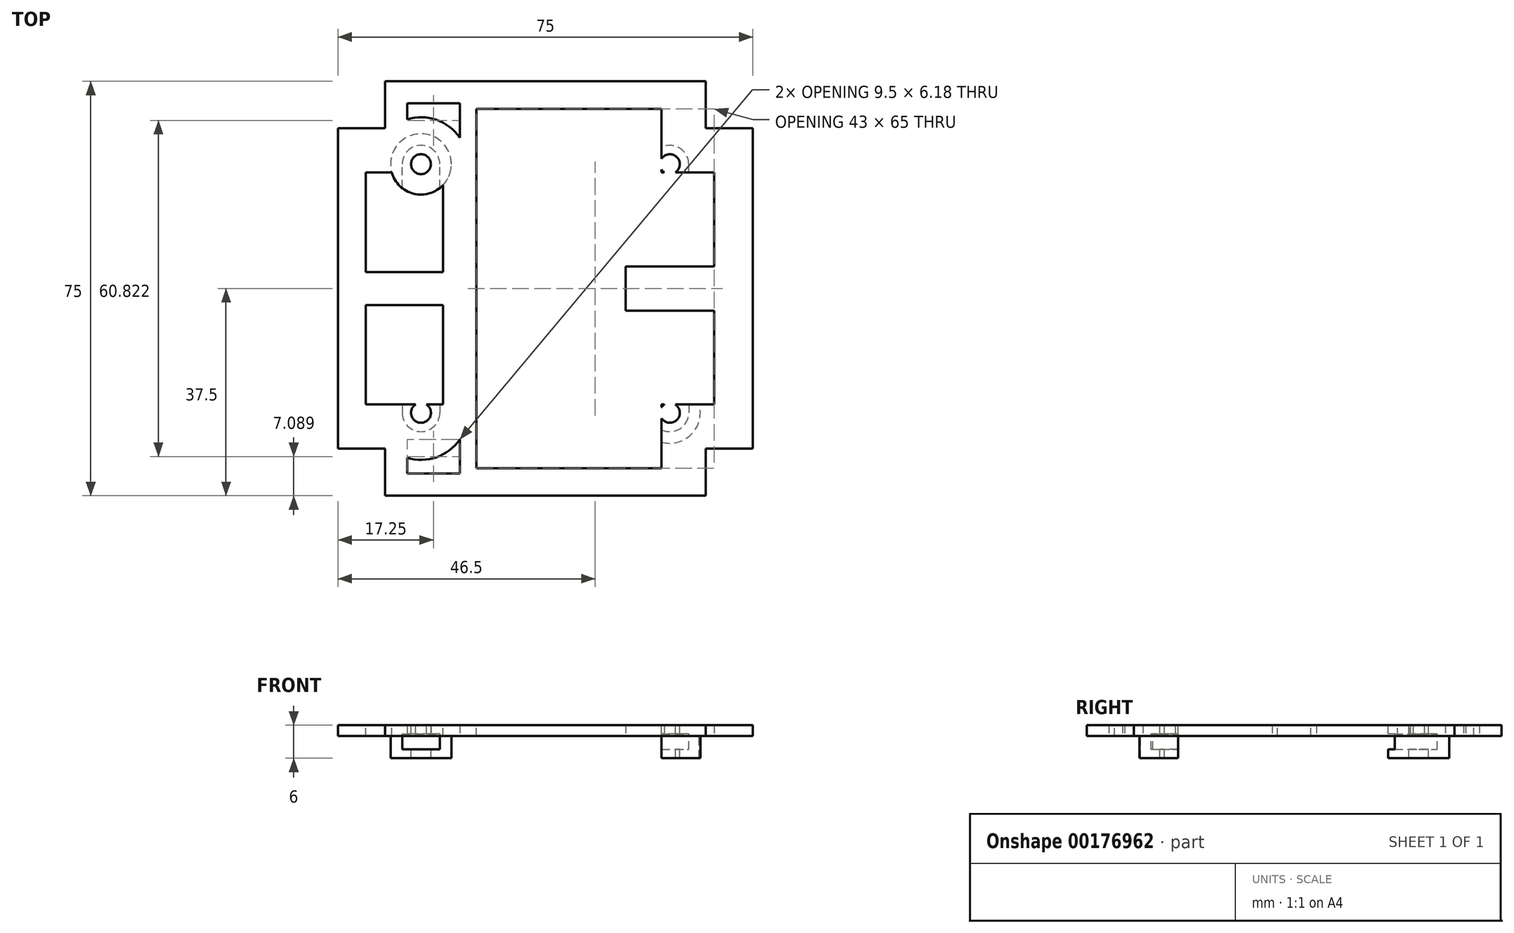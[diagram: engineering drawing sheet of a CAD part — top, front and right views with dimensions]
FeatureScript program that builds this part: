
annotation { "Feature Type Name" : "Feature", "Feature Type Description" : "" }
export const myFeature = defineFeature(function(context is Context, id is Id, definition is map)
    precondition{}
    {
        {
            assignVariable(context, id + "F0", {"name" : "thickness", "anyValue" : 2});
        }
        {
            var Q0;
            Q0=qCreatedBy(makeId("Top.planeOp"),FACE);
            var sketch = newSketch(context, id + "F1", { "sketchPlane" : qUnion([Q0])});
            skLineSegment(sketch, "E0.bottom", {"start": v(29, 37.5) * mm, "end": v(-29, 37.5) * mm});
            skLineSegment(sketch, "E0.top", {"start": v(29, -37.5) * mm, "end": v(-29, -37.5) * mm});
            skLineSegment(sketch, "E0.right", {"start": v(-37.5, 29) * mm, "end": v(-37.5, -29) * mm});
            skPoint(sketch, "E0.middle", {"position": v(0, 0) * mm});
            skLineSegment(sketch, "E1", {"start": v(-37.5, 29) * mm, "end": v(-29, 29) * mm});
            skLineSegment(sketch, "E2", {"start": v(-29, 29) * mm, "end": v(-29, 37.5) * mm});
            skLineSegment(sketch, "E3", {"start": v(0, 0) * mm, "end": v(0, 37.5) * mm, "construction": true});
            skLineSegment(sketch, "E4", {"start": v(0, 0) * mm, "end": v(50, 0) * mm, "construction": true});
            skLineSegment(sketch, "E5.MirrorCS", {"start": v(29, 29) * mm, "end": v(29, 37.5) * mm});
            skLineSegment(sketch, "E6.MirrorCS", {"start": v(37.5, 29) * mm, "end": v(29, 29) * mm});
            skLineSegment(sketch, "E7.MirrorCS", {"start": v(-37.5, -29) * mm, "end": v(-29, -29) * mm});
            skLineSegment(sketch, "E8.MirrorCS", {"start": v(-29, -29) * mm, "end": v(-29, -37.5) * mm});
            skLineSegment(sketch, "E9.MirrorCS", {"start": v(37.5, -29) * mm, "end": v(29, -29) * mm});
            skLineSegment(sketch, "E10.MirrorCS", {"start": v(37.5, -29) * mm, "end": v(37.5, 29) * mm});
            skLineSegment(sketch, "E11.MirrorCS", {"start": v(29, -29) * mm, "end": v(29, -37.5) * mm});
            skSolve(sketch);
        }
        {
            var Q0;
            Q0=makeQuery(id+"F1.imprint","IMPRINT",FACE,{"disambiguationData":[TD([[makeQuery(id+"F1.imprint","IMPRINT",EDGE,{"derivedFrom":sQuery(id+"F1.wireOp",EDGE,"E0.bottom")}),1.0]])]});
            extrude(context, id + "F2", {"entities" : qUnion([Q0]), "depth" : (getVariable(context, 'thickness')) * mm});
        }
        {
            var Q0;
            Q0=makeQuery(id+"F2.opExtrude","CAP_FACE",FACE,{"disambiguationData":[OSD([sQuery(id+"F1.wireOp",EDGE,"E0.bottom"),sQuery(id+"F1.wireOp",EDGE,"E0.right"),sQuery(id+"F1.wireOp",EDGE,"E1"),sQuery(id+"F1.wireOp",EDGE,"E2"),sQuery(id+"F1.wireOp",EDGE,"E5.MirrorCS"),sQuery(id+"F1.wireOp",EDGE,"E6.MirrorCS"),sQuery(id+"F1.wireOp",EDGE,"E7.MirrorCS"),sQuery(id+"F1.wireOp",EDGE,"E8.MirrorCS"),sQuery(id+"F1.wireOp",EDGE,"E9.MirrorCS"),sQuery(id+"F1.wireOp",EDGE,"E10.MirrorCS"),sQuery(id+"F1.wireOp",EDGE,"E11.MirrorCS"),sQuery(id+"F1.wireOp",EDGE,"E0.top"),sQuery(id+"F1.wireOp",EDGE,"QUilWeG3-0awp-yMob-JzGR-0j1FY5nFHNXd")])],"isStart":false});
            var sketch = newSketch(context, id + "F3", { "sketchPlane" : qUnion([Q0])});
            skPoint(sketch, "E12.middle", {"position": v(-6.85, 0) * mm});
            skLineSegment(sketch, "E13.bottom", {"start": v(-12.5, 12) * mm, "end": v(12.5, 12) * mm, "construction": true});
            skLineSegment(sketch, "E13.top", {"start": v(-12.5, -12) * mm, "end": v(12.5, -12) * mm, "construction": true});
            skLineSegment(sketch, "E13.left", {"start": v(-12.5, 12) * mm, "end": v(-12.5, -12) * mm, "construction": true});
            skLineSegment(sketch, "E13.right", {"start": v(12.5, 12) * mm, "end": v(12.5, -12) * mm, "construction": true});
            skPoint(sketch, "E13.middle", {"position": v(0, 0) * mm});
            skLineSegment(sketch, "E14.0", {"start": v(21, -32.5) * mm, "end": v(-12.5, -32.5) * mm});
            skLineSegment(sketch, "E15.0", {"start": v(-32.5, 21) * mm, "end": v(-32.5, 3) * mm});
            skLineSegment(sketch, "E16.0", {"start": v(-32.5, -21) * mm, "end": v(-18.5, -21) * mm});
            skLineSegment(sketch, "E17.MirrorCS", {"start": v(21, 32.5) * mm, "end": v(-12.5, 32.5) * mm});
            skLineSegment(sketch, "E18.MirrorCS", {"start": v(-32.5, 21) * mm, "end": v(-18.5, 21) * mm});
            skLineSegment(sketch, "E19.MirrorCS", {"start": v(30.5, 21) * mm, "end": v(30.5, -21) * mm});
            skLineSegment(sketch, "E20.MirrorCS", {"start": v(30.5, -21) * mm, "end": v(21, -21) * mm});
            skLineSegment(sketch, "E21.MirrorCS", {"start": v(21, -21) * mm, "end": v(21, -32.5) * mm});
            skLineSegment(sketch, "E22", {"start": v(-12.5, -32.5) * mm, "end": v(-12.5, 32.5) * mm});
            skLineSegment(sketch, "E23.0", {"start": v(-18.5, -21) * mm, "end": v(-18.5, -3) * mm});
            skLineSegment(sketch, "E24", {"start": v(-32.5, 3) * mm, "end": v(-18.5, 3) * mm});
            skLineSegment(sketch, "E25.MirrorCS", {"start": v(-32.5, -3) * mm, "end": v(-18.5, -3) * mm});
            skLineSegment(sketch, "E26.trimOffspring", {"start": v(-18.5, 3) * mm, "end": v(-18.5, 21) * mm});
            skLineSegment(sketch, "E27.trimOffspring", {"start": v(-32.5, -3) * mm, "end": v(-32.5, -21) * mm});
            skLineSegment(sketch, "E28.MirrorCS", {"start": v(30.5, 21) * mm, "end": v(21, 21) * mm});
            skLineSegment(sketch, "E29.MirrorCS", {"start": v(21, 21) * mm, "end": v(21, 32.5) * mm});
            skSolve(sketch);
        }
        {
            var Q0;
            Q0=makeQuery(id+"F3.imprint","IMPRINT",FACE,{"disambiguationData":[TD([[makeQuery(id+"F3.imprint","IMPRINT",EDGE,{"derivedFrom":sQuery(id+"F3.wireOp",EDGE,"E15.0")}),1.0]])]});
            var Q1;
            Q1=makeQuery(id+"F3.imprint","IMPRINT",FACE,{"disambiguationData":[TD([[makeQuery(id+"F3.imprint","IMPRINT",EDGE,{"derivedFrom":sQuery(id+"F3.wireOp",EDGE,"E16.0")}),1.0]])]});
            var Q2;
            Q2=makeQuery(id+"F3.imprint","IMPRINT",FACE,{"disambiguationData":[TD([[makeQuery(id+"F3.imprint","IMPRINT",EDGE,{"derivedFrom":sQuery(id+"F3.wireOp",EDGE,"E14.0")}),-1.0]])]});
            extrude(context, id + "F4", {"entities" : qUnion([Q0, Q1, Q2]), "operationType" : NewBodyOperationType.REMOVE, "endBound" : BoundingType.THROUGH_ALL, "oppositeDirection" : true, "depth" : 25 * mm});
        }
        {
            var Q0;
            Q0=makeQuery(id+"F2.opExtrude","CAP_FACE",FACE,{"disambiguationData":[OSD([sQuery(id+"F1.wireOp",EDGE,"E0.bottom"),sQuery(id+"F1.wireOp",EDGE,"E0.right"),sQuery(id+"F1.wireOp",EDGE,"E1"),sQuery(id+"F1.wireOp",EDGE,"E2"),sQuery(id+"F1.wireOp",EDGE,"E5.MirrorCS"),sQuery(id+"F1.wireOp",EDGE,"E6.MirrorCS"),sQuery(id+"F1.wireOp",EDGE,"E7.MirrorCS"),sQuery(id+"F1.wireOp",EDGE,"E8.MirrorCS"),sQuery(id+"F1.wireOp",EDGE,"E9.MirrorCS"),sQuery(id+"F1.wireOp",EDGE,"E10.MirrorCS"),sQuery(id+"F1.wireOp",EDGE,"E11.MirrorCS"),sQuery(id+"F1.wireOp",EDGE,"E0.top"),sQuery(id+"F1.wireOp",EDGE,"QUilWeG3-0awp-yMob-JzGR-0j1FY5nFHNXd")])],"isStart":false});
            var sketch = newSketch(context, id + "F5", { "sketchPlane" : qUnion([Q0])});
            skCircle(sketch, "E30", {"center": v(-22.5, 22.5) * mm, "radius": 1.8 * mm});
            skCircle(sketch, "E31", {"center": v(-22.5, 22.5) * mm, "radius": 5.5 * mm});
            skCircle(sketch, "E32.MirrorC", {"center": v(-22.5, -22.5) * mm, "radius": 1.8 * mm});
            skCircle(sketch, "E33.MirrorC", {"center": v(-22.5, -22.5) * mm, "radius": 5.5 * mm});
            skCircle(sketch, "E34.MirrorC", {"center": v(22.5, 22.5) * mm, "radius": 1.8 * mm});
            skCircle(sketch, "E35.MirrorC", {"center": v(22.5, 22.5) * mm, "radius": 5.5 * mm});
            skCircle(sketch, "E36.MirrorC", {"center": v(22.5, -22.5) * mm, "radius": 5.5 * mm});
            skCircle(sketch, "E37.MirrorC", {"center": v(22.5, -22.5) * mm, "radius": 1.8 * mm});
            skSolve(sketch);
        }
        {
            var Q0;
            {var subQ0=makeQuery(id+"F4.boolean.opBoolean","COPY",EDGE,{"derivedFrom":makeQuery(id+"F4.opExtrude","CAP_EDGE",EDGE,{"disambiguationData":[OSD([sQuery(id+"F3.wireOp",EDGE,"E18.MirrorCS")])],"isStart":true})});var subQ3=sQuery(id+"F5.wireOp",EDGE,"E30");var subQ9=makeQuery(id+"F5.imprint","INTERSECT",VERTEX,{"disambiguationData":[OD(0.0)],"derivedFrom":[subQ0,subQ3]});Q0=makeQuery(id+"F5.imprint","IMPRINT",FACE,{"disambiguationData":[TD([[makeQuery(id+"F5.imprint","IMPRINT",EDGE,{"disambiguationData":[TD([[subQ9,-1.0]])],"derivedFrom":subQ3}),-1.0]])]});}
            var Q1;
            {var subQ0=sQuery(id+"F5.wireOp",EDGE,"E30");var subQ1=makeQuery(id+"F4.boolean.opBoolean","COPY",EDGE,{"derivedFrom":makeQuery(id+"F4.opExtrude","CAP_EDGE",EDGE,{"disambiguationData":[OSD([sQuery(id+"F3.wireOp",EDGE,"E18.MirrorCS")])],"isStart":true})});var subQ2=makeQuery(id+"F5.imprint","INTERSECT",VERTEX,{"disambiguationData":[OD(0.0)],"derivedFrom":[subQ1,subQ0]});Q1=makeQuery(id+"F5.imprint","IMPRINT",FACE,{"disambiguationData":[TD([[makeQuery(id+"F5.imprint","IMPRINT",EDGE,{"disambiguationData":[TD([[subQ2,1.0]])],"derivedFrom":subQ0}),-1.0]])]});}
            var Q2;
            {var subQ0=sQuery(id+"F5.wireOp",EDGE,"E30");var subQ1=makeQuery(id+"F4.boolean.opBoolean","COPY",EDGE,{"derivedFrom":makeQuery(id+"F4.opExtrude","CAP_EDGE",EDGE,{"disambiguationData":[OSD([sQuery(id+"F3.wireOp",EDGE,"E18.MirrorCS")])],"isStart":true})});var subQ2=makeQuery(id+"F5.imprint","INTERSECT",VERTEX,{"disambiguationData":[OD(1.0)],"derivedFrom":[subQ1,subQ0]});Q2=makeQuery(id+"F5.imprint","IMPRINT",FACE,{"disambiguationData":[TD([[makeQuery(id+"F5.imprint","IMPRINT",EDGE,{"disambiguationData":[TD([[subQ2,-1.0]])],"derivedFrom":subQ0}),-1.0]])]});}
            var Q3;
            {var subQ0=sQuery(id+"F5.wireOp",EDGE,"E32.MirrorC");var subQ1=makeQuery(id+"F4.boolean.opBoolean","COPY",EDGE,{"derivedFrom":makeQuery(id+"F4.opExtrude","CAP_EDGE",EDGE,{"disambiguationData":[OSD([sQuery(id+"F3.wireOp",EDGE,"E16.0")])],"isStart":true})});var subQ2=makeQuery(id+"F5.imprint","INTERSECT",VERTEX,{"disambiguationData":[OD(0.0)],"derivedFrom":[subQ1,subQ0]});Q3=makeQuery(id+"F5.imprint","IMPRINT",FACE,{"disambiguationData":[TD([[makeQuery(id+"F5.imprint","IMPRINT",EDGE,{"disambiguationData":[TD([[subQ2,1.0]])],"derivedFrom":subQ0}),1.0]])]});}
            var Q4;
            {var subQ0=sQuery(id+"F5.wireOp",EDGE,"E32.MirrorC");var subQ1=makeQuery(id+"F4.boolean.opBoolean","COPY",EDGE,{"derivedFrom":makeQuery(id+"F4.opExtrude","CAP_EDGE",EDGE,{"disambiguationData":[OSD([sQuery(id+"F3.wireOp",EDGE,"E16.0")])],"isStart":true})});var subQ2=makeQuery(id+"F5.imprint","INTERSECT",VERTEX,{"disambiguationData":[OD(1.0)],"derivedFrom":[subQ1,subQ0]});Q4=makeQuery(id+"F5.imprint","IMPRINT",FACE,{"disambiguationData":[TD([[makeQuery(id+"F5.imprint","IMPRINT",EDGE,{"disambiguationData":[TD([[subQ2,-1.0]])],"derivedFrom":subQ0}),1.0]])]});}
            var Q5;
            {var subQ3=makeQuery(id+"F4.boolean.opBoolean","COPY",EDGE,{"derivedFrom":makeQuery(id+"F4.opExtrude","CAP_EDGE",EDGE,{"disambiguationData":[OSD([sQuery(id+"F3.wireOp",EDGE,"E16.0")])],"isStart":true})});var subQ5=sQuery(id+"F5.wireOp",EDGE,"E32.MirrorC");var subQ9=makeQuery(id+"F5.imprint","INTERSECT",VERTEX,{"disambiguationData":[OD(0.0)],"derivedFrom":[subQ3,subQ5]});Q5=makeQuery(id+"F5.imprint","IMPRINT",FACE,{"disambiguationData":[TD([[makeQuery(id+"F5.imprint","IMPRINT",EDGE,{"disambiguationData":[TD([[subQ9,-1.0]])],"derivedFrom":subQ5}),1.0]])]});}
            var Q6;
            {var subQ0=sQuery(id+"F5.wireOp",EDGE,"E36.MirrorC");var subQ1=makeQuery(id+"F4.boolean.opBoolean","COPY",EDGE,{"derivedFrom":makeQuery(id+"F4.opExtrude","CAP_EDGE",EDGE,{"disambiguationData":[OSD([sQuery(id+"F3.wireOp",EDGE,"E20.MirrorCS")])],"isStart":true})});var subQ2=makeQuery(id+"F5.imprint","INTERSECT",VERTEX,{"derivedFrom":[subQ1,subQ0]});Q6=makeQuery(id+"F5.imprint","IMPRINT",FACE,{"disambiguationData":[TD([[makeQuery(id+"F5.imprint","IMPRINT",EDGE,{"disambiguationData":[TD([[subQ2,1.0]])],"derivedFrom":subQ0}),1.0]])]});}
            var Q7;
            {var subQ0=sQuery(id+"F5.wireOp",EDGE,"E37.MirrorC");var subQ1=makeQuery(id+"F4.boolean.opBoolean","COPY",EDGE,{"derivedFrom":makeQuery(id+"F4.opExtrude","CAP_EDGE",EDGE,{"disambiguationData":[OSD([sQuery(id+"F3.wireOp",EDGE,"E20.MirrorCS")])],"isStart":true})});var subQ2=makeQuery(id+"F5.imprint","INTERSECT",VERTEX,{"disambiguationData":[OD(1.0)],"derivedFrom":[subQ1,subQ0]});Q7=makeQuery(id+"F5.imprint","IMPRINT",FACE,{"disambiguationData":[TD([[makeQuery(id+"F5.imprint","IMPRINT",EDGE,{"disambiguationData":[TD([[subQ2,-1.0]])],"derivedFrom":subQ0}),-1.0]])]});}
            var Q8;
            {var subQ4=makeQuery(id+"F4.boolean.opBoolean","COPY",EDGE,{"derivedFrom":makeQuery(id+"F4.opExtrude","CAP_EDGE",EDGE,{"disambiguationData":[OSD([sQuery(id+"F3.wireOp",EDGE,"E20.MirrorCS")])],"isStart":true})});var subQ8=sQuery(id+"F5.wireOp",EDGE,"E36.MirrorC");var subQ9=makeQuery(id+"F5.imprint","INTERSECT",VERTEX,{"derivedFrom":[subQ4,subQ8]});Q8=makeQuery(id+"F5.imprint","IMPRINT",FACE,{"disambiguationData":[TD([[makeQuery(id+"F5.imprint","IMPRINT",EDGE,{"disambiguationData":[TD([[subQ9,-1.0]])],"derivedFrom":subQ8}),1.0]])]});}
            var Q9;
            {var subQ0=makeQuery(id+"F4.boolean.opBoolean","COPY",EDGE,{"derivedFrom":makeQuery(id+"F4.opExtrude","CAP_EDGE",EDGE,{"disambiguationData":[OSD([sQuery(id+"F3.wireOp",EDGE,"23c06a62-adb4-41f1-888d-e85a26099f890.MirrorCS")])],"isStart":true})});var subQ3=sQuery(id+"F5.wireOp",EDGE,"E34.MirrorC");var subQ9=makeQuery(id+"F5.imprint","INTERSECT",VERTEX,{"disambiguationData":[OD(0.0)],"derivedFrom":[subQ0,subQ3]});Q9=makeQuery(id+"F5.imprint","IMPRINT",FACE,{"disambiguationData":[TD([[makeQuery(id+"F5.imprint","IMPRINT",EDGE,{"disambiguationData":[TD([[subQ9,-1.0]])],"derivedFrom":subQ3}),1.0]])]});}
            var Q10;
            {var subQ0=sQuery(id+"F5.wireOp",EDGE,"E34.MirrorC");var subQ1=makeQuery(id+"F4.boolean.opBoolean","COPY",EDGE,{"derivedFrom":makeQuery(id+"F4.opExtrude","CAP_EDGE",EDGE,{"disambiguationData":[OSD([sQuery(id+"F3.wireOp",EDGE,"23c06a62-adb4-41f1-888d-e85a26099f890.MirrorCS")])],"isStart":true})});var subQ2=makeQuery(id+"F5.imprint","INTERSECT",VERTEX,{"disambiguationData":[OD(0.0)],"derivedFrom":[subQ1,subQ0]});Q10=makeQuery(id+"F5.imprint","IMPRINT",FACE,{"disambiguationData":[TD([[makeQuery(id+"F5.imprint","IMPRINT",EDGE,{"disambiguationData":[TD([[subQ2,1.0]])],"derivedFrom":subQ0}),1.0]])]});}
            var Q11;
            {var subQ0=sQuery(id+"F5.wireOp",EDGE,"E34.MirrorC");var subQ1=makeQuery(id+"F4.boolean.opBoolean","COPY",EDGE,{"derivedFrom":makeQuery(id+"F4.opExtrude","CAP_EDGE",EDGE,{"disambiguationData":[OSD([sQuery(id+"F3.wireOp",EDGE,"23c06a62-adb4-41f1-888d-e85a26099f890.MirrorCS")])],"isStart":true})});var subQ2=makeQuery(id+"F5.imprint","INTERSECT",VERTEX,{"disambiguationData":[OD(1.0)],"derivedFrom":[subQ1,subQ0]});Q11=makeQuery(id+"F5.imprint","IMPRINT",FACE,{"disambiguationData":[TD([[makeQuery(id+"F5.imprint","IMPRINT",EDGE,{"disambiguationData":[TD([[subQ2,-1.0]])],"derivedFrom":subQ0}),1.0]])]});}
            var Q12;
            {var subQ1=makeQuery(id+"F4.boolean.opBoolean","COPY",EDGE,{"derivedFrom":makeQuery(id+"F4.opExtrude","CAP_EDGE",EDGE,{"disambiguationData":[OSD([sQuery(id+"F3.wireOp",EDGE,"E28.MirrorCS")])],"isStart":true})});var subQ3=sQuery(id+"F5.wireOp",EDGE,"E34.MirrorC");var subQ10=makeQuery(id+"F5.imprint","INTERSECT",VERTEX,{"disambiguationData":[OD(0.0)],"derivedFrom":[subQ1,subQ3]});Q12=makeQuery(id+"F5.imprint","IMPRINT",FACE,{"disambiguationData":[TD([[makeQuery(id+"F5.imprint","IMPRINT",EDGE,{"disambiguationData":[TD([[subQ10,-1.0]])],"derivedFrom":subQ3}),1.0]])]});}
            extrude(context, id + "F6", {"entities" : qUnion([Q0, Q1, Q2, Q3, Q4, Q5, Q6, Q7, Q8, Q9, Q10, Q11, Q12]), "operationType" : NewBodyOperationType.ADD, "oppositeDirection" : true, "depth" : 6 * mm});
        }
        {
            var Q0;
            Q0=makeQuery(id+"F6.opExtrude","CAP_FACE",FACE,{"disambiguationData":[OSD([sQuery(id+"F5.wireOp",EDGE,"E30"),sQuery(id+"F5.wireOp",EDGE,"E31")])],"isStart":false});
            var sketch = newSketch(context, id + "F7", { "sketchPlane" : qUnion([Q0])});
            skCircle(sketch, "E38", {"center": v(-22.5, -22.5) * mm, "radius": 1.8 * mm});
            skCircle(sketch, "E39.MirrorC", {"center": v(-22.5, 22.5) * mm, "radius": 1.8 * mm});
            skCircle(sketch, "E40.MirrorC", {"center": v(22.5, -22.5) * mm, "radius": 1.8 * mm});
            skCircle(sketch, "E41.MirrorC", {"center": v(22.5, 22.5) * mm, "radius": 1.8 * mm});
            skSolve(sketch);
        }
        {
            var Q0;
            Q0=qSketchRegion(id+"F7",true);
            extrude(context, id + "F8", {"entities" : qUnion([Q0]), "operationType" : NewBodyOperationType.REMOVE, "endBound" : BoundingType.THROUGH_ALL, "oppositeDirection" : true, "depth" : 25 * mm});
        }
        {
            var Q0;
            {var subQ8=sQuery(id+"F1.wireOp",EDGE,"E1");var subQ9=sQuery(id+"F1.wireOp",EDGE,"E9.MirrorCS");var subQ10=sQuery(id+"F5.wireOp",EDGE,"E31");var subQ11=sQuery(id+"F1.wireOp",EDGE,"E0.top");var subQ12=sQuery(id+"F1.wireOp",EDGE,"E10.MirrorCS");var subQ13=sQuery(id+"F1.wireOp",EDGE,"E11.MirrorCS");var subQ14=sQuery(id+"F1.wireOp",EDGE,"E2");var subQ15=sQuery(id+"F1.wireOp",EDGE,"E0.right");var subQ16=sQuery(id+"F1.wireOp",EDGE,"E0.bottom");var subQ17=sQuery(id+"F1.wireOp",EDGE,"E5.MirrorCS");var subQ18=sQuery(id+"F5.wireOp",EDGE,"E33.MirrorC");var subQ19=sQuery(id+"F1.wireOp",EDGE,"E6.MirrorCS");var subQ20=sQuery(id+"F1.wireOp",EDGE,"E7.MirrorCS");var subQ21=sQuery(id+"F1.wireOp",EDGE,"E8.MirrorCS");var subQ22=sQuery(id+"F5.wireOp",EDGE,"E37.MirrorC");var subQ23=sQuery(id+"F5.wireOp",EDGE,"E30");var subQ24=sQuery(id+"F5.wireOp",EDGE,"E32.MirrorC");var subQ25=sQuery(id+"F5.wireOp",EDGE,"E36.MirrorC");Q0=makeQuery(id+"F8.boolean.opBoolean","SPLIT",FACE,{"disambiguationData":[TD([makeQuery(id+"F2.opExtrude","SWEPT_FACE",FACE,{"disambiguationData":[OSD([subQ16])]})])],"derivedFrom":makeQuery(id+"F6.boolean.opBoolean","MERGE",FACE,{"derivedFrom":[makeQuery(id+"F2.opExtrude","CAP_FACE",FACE,{"disambiguationData":[OSD([subQ16,subQ15,subQ8,subQ14,subQ17,subQ19,subQ20,subQ21,subQ9,subQ12,subQ13,subQ11])],"isStart":false}),makeQuery(id+"F6.opExtrude","CAP_FACE",FACE,{"disambiguationData":[OSD([subQ23,subQ10])],"isStart":true}),makeQuery(id+"F6.opExtrude","CAP_FACE",FACE,{"disambiguationData":[OSD([subQ24,subQ18])],"isStart":true}),makeQuery(id+"F6.opExtrude","CAP_FACE",FACE,{"disambiguationData":[OSD([subQ25,subQ22])],"isStart":true})]})});}
            cPlane(context, id + "F9", {"entities" : qUnion([Q0]), "cplaneType" : CPlaneType.OFFSET, "offset" : 3 * mm, "oppositeDirection" : true, "width" : 150 * mm, "height" : 150 * mm});
        }
        {
            var Q0;
            Q0=qCreatedBy(id+"F9.planeOp",FACE);
            var sketch = newSketch(context, id + "F10", { "sketchPlane" : qUnion([Q0])});
            skCircle(sketch, "E42", {"center": v(22.5, -22.5) * mm, "radius": 3.4 * mm});
            skCircle(sketch, "E43.MirrorC", {"center": v(22.5, 22.5) * mm, "radius": 3.4 * mm});
            skCircle(sketch, "E44.MirrorC", {"center": v(-22.5, -22.5) * mm, "radius": 3.4 * mm});
            skCircle(sketch, "E45.MirrorC", {"center": v(-22.5, 22.5) * mm, "radius": 3.4 * mm});
            skSolve(sketch);
        }
        {
            var Q0;
            Q0 = qSketchRegion(id + "F10", true);
            extrude(context, id + "F11", {"entities" : qUnion([Q0]), "operationType" : NewBodyOperationType.REMOVE, "oppositeDirection" : true, "depth" : 1.4 * mm, "hasSecondDirection" : true, "secondDirectionOppositeDirection" : false, "secondDirectionDepth" : 1.4 * mm});
        }
        {
            var Q0;
            Q0=qCreatedBy(makeId("Front.planeOp"),FACE);
            cPlane(context, id + "F12", {"entities" : qUnion([Q0]), "cplaneType" : CPlaneType.OFFSET, "offset" : 22.5 * mm, "width" : 150 * mm, "height" : 150 * mm});
        }
        {
            var Q0;
            Q0=qCreatedBy(id+"F12.planeOp",FACE);
            var sketch = newSketch(context, id + "F13", { "sketchPlane" : qUnion([Q0])});
            skLineSegment(sketch, "E46.bottom", {"start": v(19.1, 0.4) * mm, "end": v(25.9, 0.4) * mm});
            skLineSegment(sketch, "E46.top", {"start": v(19.1, -2.4) * mm, "end": v(25.9, -2.4) * mm});
            skLineSegment(sketch, "E46.left", {"start": v(19.1, 0.4) * mm, "end": v(19.1, -2.4) * mm});
            skLineSegment(sketch, "E46.right", {"start": v(25.9, 0.4) * mm, "end": v(25.9, -2.4) * mm});
            skPoint(sketch, "E46.middle", {"position": v(22.5, -1) * mm});
            skLineSegment(sketch, "E47", {"start": v(22.5, 2) * mm, "end": v(22.5, -4) * mm, "construction": true});
            skLineSegment(sketch, "E48.MirrorCS", {"start": v(-25.9, 0.4) * mm, "end": v(-25.9, -2.4) * mm});
            skPoint(sketch, "E49.MirrorP", {"position": v(-22.5, -1) * mm});
            skLineSegment(sketch, "E50.MirrorCS", {"start": v(-19.1, 0.4) * mm, "end": v(-25.9, 0.4) * mm});
            skLineSegment(sketch, "E51.MirrorCS", {"start": v(-22.5, 2) * mm, "end": v(-22.5, -4) * mm, "construction": true});
            skLineSegment(sketch, "E52.MirrorCS", {"start": v(-19.1, -2.4) * mm, "end": v(-25.9, -2.4) * mm});
            skLineSegment(sketch, "E53.MirrorCS", {"start": v(-19.1, 0.4) * mm, "end": v(-19.1, -2.4) * mm});
            skSolve(sketch);
        }
        {
            var Q0;
            Q0 = qSketchRegion(id + "F13", true);
            extrude(context, id + "F14", {"entities" : qUnion([Q0]), "operationType" : NewBodyOperationType.REMOVE, "oppositeDirection" : true, "depth" : 8.8 * mm});
        }
        {
            var Q0;
            Q0=qCreatedBy(makeId("Front.planeOp"),FACE);
            cPlane(context, id + "F15", {"entities" : qUnion([Q0]), "cplaneType" : CPlaneType.OFFSET, "offset" : 22.5 * mm, "oppositeDirection" : true, "width" : 150 * mm, "height" : 150 * mm});
        }
        {
            var Q0;
            Q0=qCreatedBy(id+"F15.planeOp",FACE);
            var sketch = newSketch(context, id + "F16", { "sketchPlane" : qUnion([Q0])});
            skLineSegment(sketch, "E54", {"start": v(22.5, 2) * mm, "end": v(22.5, -4) * mm, "construction": true});
            skLineSegment(sketch, "E55.bottom", {"start": v(25.9, 0.4) * mm, "end": v(19.1, 0.4) * mm});
            skLineSegment(sketch, "E55.top", {"start": v(25.9, -2.4) * mm, "end": v(19.1, -2.4) * mm});
            skLineSegment(sketch, "E55.left", {"start": v(25.9, 0.4) * mm, "end": v(25.9, -2.4) * mm});
            skLineSegment(sketch, "E55.right", {"start": v(19.1, 0.4) * mm, "end": v(19.1, -2.4) * mm});
            skPoint(sketch, "E55.middle", {"position": v(22.5, -1) * mm});
            skLineSegment(sketch, "E56.MirrorCS", {"start": v(-25.9, -2.4) * mm, "end": v(-19.1, -2.4) * mm});
            skLineSegment(sketch, "E57.MirrorCS", {"start": v(-19.1, 0.4) * mm, "end": v(-19.1, -2.4) * mm});
            skLineSegment(sketch, "E58.MirrorCS", {"start": v(-22.5, 2) * mm, "end": v(-22.5, -4) * mm, "construction": true});
            skPoint(sketch, "E59.MirrorP", {"position": v(-22.5, -1) * mm});
            skLineSegment(sketch, "E60.MirrorCS", {"start": v(-25.9, 0.4) * mm, "end": v(-19.1, 0.4) * mm});
            skLineSegment(sketch, "E61.MirrorCS", {"start": v(-25.9, 0.4) * mm, "end": v(-25.9, -2.4) * mm});
            skSolve(sketch);
        }
        {
            var Q0;
            Q0 = qSketchRegion(id + "F16", true);
            extrude(context, id + "F17", {"entities" : qUnion([Q0]), "operationType" : NewBodyOperationType.REMOVE, "depth" : 10.3 * mm});
        }
        {
            var Q0;
            Q0=makeQuery(id+"F4.boolean.opBoolean","COPY",FACE,{"derivedFrom":makeQuery(id+"F4.opExtrude","SWEPT_FACE",FACE,{"disambiguationData":[OSD([sQuery(id+"F3.wireOp",EDGE,"E19.MirrorCS")])]})});
            var sketch = newSketch(context, id + "F18", { "sketchPlane" : qUnion([Q0])});
            skLineSegment(sketch, "E62", {"start": v(0, 0) * mm, "end": v(0, 2) * mm, "construction": true});
            skLineSegment(sketch, "E63.bottom", {"start": v(-4, 2) * mm, "end": v(4, 2) * mm});
            skLineSegment(sketch, "E63.top", {"start": v(-4, 0) * mm, "end": v(4, 0) * mm});
            skLineSegment(sketch, "E63.left", {"start": v(-4, 2) * mm, "end": v(-4, 0) * mm});
            skLineSegment(sketch, "E63.right", {"start": v(4, 2) * mm, "end": v(4, 0) * mm});
            skPoint(sketch, "E63.middle", {"position": v(0, 1) * mm});
            skSolve(sketch);
        }
        {
            var Q0;
            Q0 = qSketchRegion(id + "F18", true);
            extrude(context, id + "F19", {"entities" : qUnion([Q0]), "operationType" : NewBodyOperationType.ADD, "depth" : 16 * mm});
        }
        {
            var Q0;
            {var subQ0=sQuery(id+"F1.wireOp",EDGE,"E1");var subQ1=sQuery(id+"F1.wireOp",EDGE,"E9.MirrorCS");var subQ2=sQuery(id+"F1.wireOp",EDGE,"E0.top");var subQ3=sQuery(id+"F1.wireOp",EDGE,"E10.MirrorCS");var subQ4=sQuery(id+"F1.wireOp",EDGE,"E11.MirrorCS");var subQ5=sQuery(id+"F1.wireOp",EDGE,"E2");var subQ6=sQuery(id+"F1.wireOp",EDGE,"E0.right");var subQ7=sQuery(id+"F1.wireOp",EDGE,"E0.bottom");var subQ8=sQuery(id+"F1.wireOp",EDGE,"E5.MirrorCS");var subQ9=sQuery(id+"F1.wireOp",EDGE,"E6.MirrorCS");var subQ10=sQuery(id+"F1.wireOp",EDGE,"E7.MirrorCS");var subQ11=sQuery(id+"F1.wireOp",EDGE,"E8.MirrorCS");Q0=makeQuery(id+"F19.boolean.opBoolean","MERGE",FACE,{"derivedFrom":[makeQuery(id+"F6.boolean.opBoolean","SPLIT",FACE,{"disambiguationData":[TD([makeQuery(id+"F2.opExtrude","SWEPT_FACE",FACE,{"disambiguationData":[OSD([subQ7])]})])],"derivedFrom":makeQuery(id+"F2.opExtrude","CAP_FACE",FACE,{"disambiguationData":[OSD([subQ7,subQ6,subQ0,subQ5,subQ8,subQ9,subQ10,subQ11,subQ1,subQ3,subQ4,subQ2])],"isStart":true})}),makeQuery(id+"F19.opExtrude","SWEPT_FACE",FACE,{"disambiguationData":[OSD([sQuery(id+"F18.wireOp",EDGE,"E63.top")])]})]});}
            var sketch = newSketch(context, id + "F20", { "sketchPlane" : qUnion([Q0])});
            skArc(sketch, "E64.0", {"start": v(-15.5, 27.32) * mm, "mid": v(-19.7, 30.53) * mm, "end": v(-25, 30.62) * mm});
            skLineSegment(sketch, "E65.0", {"start": v(-15.5, 33.5) * mm, "end": v(-15.5, 27.32) * mm});
            skLineSegment(sketch, "E66.0", {"start": v(-15.5, 33.5) * mm, "end": v(-25, 33.5) * mm});
            skLineSegment(sketch, "E67.0", {"start": v(-25, 30.62) * mm, "end": v(-25, 33.5) * mm});
            skLineSegment(sketch, "E68.MirrorCS", {"start": v(-15.5, -33.5) * mm, "end": v(-25, -33.5) * mm});
            skLineSegment(sketch, "E69.MirrorCS", {"start": v(-15.5, -33.5) * mm, "end": v(-15.5, -27.32) * mm});
            skLineSegment(sketch, "E70.MirrorCS", {"start": v(-25, -30.62) * mm, "end": v(-25, -33.5) * mm});
            skArc(sketch, "E71.MirrorCS", {"start": v(-15.5, -27.32) * mm, "mid": v(-19.7, -30.53) * mm, "end": v(-25, -30.62) * mm});
            skSolve(sketch);
        }
        {
            var Q0;
            Q0=makeQuery(id+"F20.imprint","IMPRINT",FACE,{"disambiguationData":[TD([[makeQuery(id+"F20.imprint","IMPRINT",EDGE,{"derivedFrom":sQuery(id+"F20.wireOp",EDGE,"E64.0")}),-1.0]])]});
            var Q1;
            Q1=makeQuery(id+"F20.imprint","IMPRINT",FACE,{"disambiguationData":[TD([[makeQuery(id+"F20.imprint","IMPRINT",EDGE,{"derivedFrom":sQuery(id+"F20.wireOp",EDGE,"E68.MirrorCS")}),-1.0]])]});
            extrude(context, id + "F21", {"entities" : qUnion([Q0, Q1]), "operationType" : NewBodyOperationType.REMOVE, "endBound" : BoundingType.THROUGH_ALL, "oppositeDirection" : true, "depth" : 25 * mm});
        }
    });
